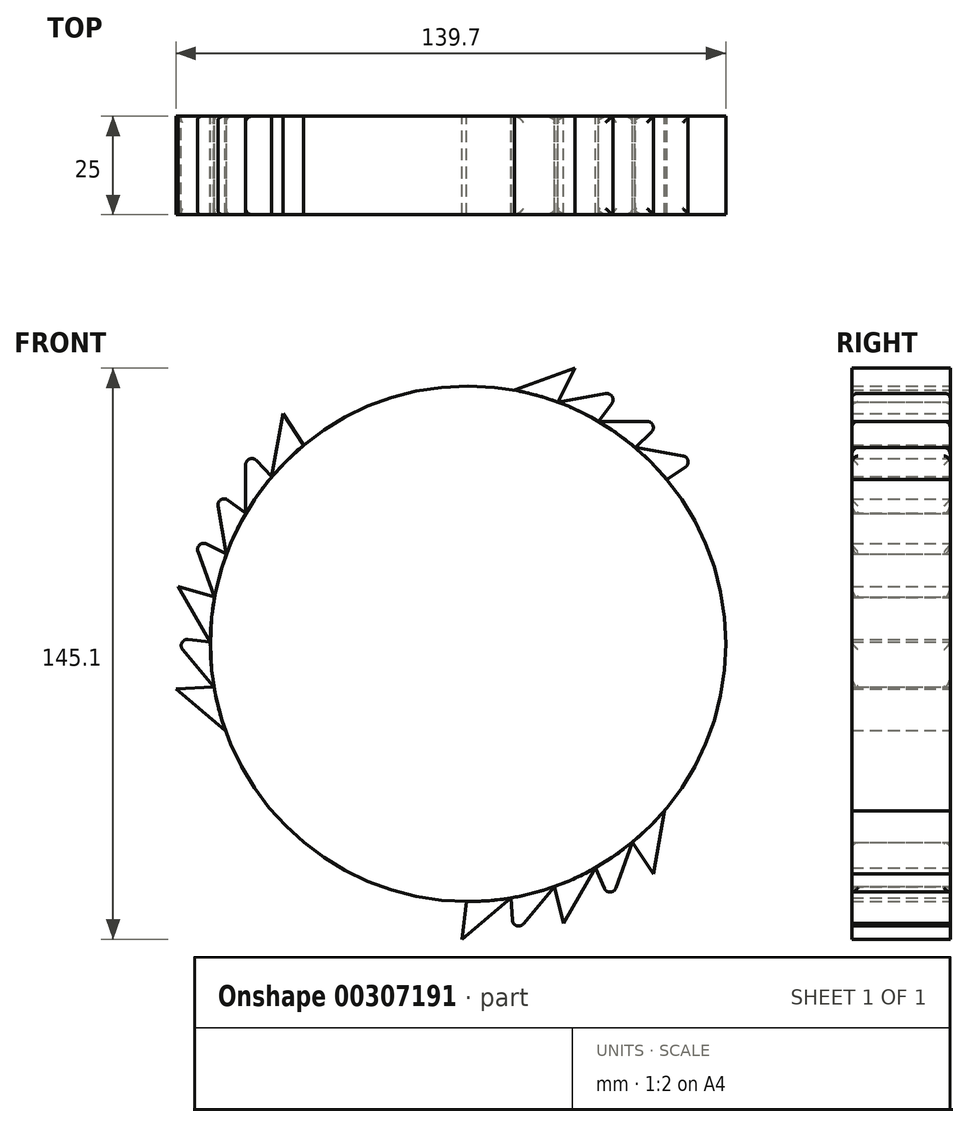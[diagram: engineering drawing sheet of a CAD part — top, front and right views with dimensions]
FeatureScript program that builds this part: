
annotation { "Feature Type Name" : "Feature", "Feature Type Description" : "" }
export const myFeature = defineFeature(function(context is Context, id is Id, definition is map)
    precondition{}
    {
        {
            var Q0;
            Q0=qCreatedBy(makeId("Front.planeOp"),FACE);
            var sketch = newSketch(context, id + "F0", { "sketchPlane" : qUnion([Q0])});
            skCircle(sketch, "E0", {"center": v(0, 0) * mm, "radius": 65.49 * mm});
            skLineSegment(sketch, "E1", {"start": v(33.09, 56.51) * mm, "end": v(49.45, 56.51) * mm});
            skLineSegment(sketch, "E2", {"start": v(49.45, 56.51) * mm, "end": v(42.44, 49.87) * mm});
            skLineSegment(sketch, "E3.1.1", {"start": v(-73.67, 14.57) * mm, "end": v(-64.4, 11.82) * mm});
            skLineSegment(sketch, "E3.1.2", {"start": v(-65.48, 0.4) * mm, "end": v(-73.67, 14.57) * mm});
            skLineSegment(sketch, "E3.2.1", {"start": v(24.21, -71.08) * mm, "end": v(21.97, -61.7) * mm});
            skLineSegment(sketch, "E3.2.2", {"start": v(32.4, -56.91) * mm, "end": v(24.21, -71.08) * mm});
            skLineSegment(sketch, "E4.1.0", {"start": v(38.89, 64.24) * mm, "end": v(33.14, 56.48) * mm});
            skLineSegment(sketch, "E4.1.1", {"start": v(22.77, 61.4) * mm, "end": v(38.89, 64.24) * mm});
            skLineSegment(sketch, "E4.1.3", {"start": v(-64.56, -10.98) * mm, "end": v(-75.08, 1.56) * mm});
            skLineSegment(sketch, "E4.1.5", {"start": v(41.79, -50.42) * mm, "end": v(36.19, -65.8) * mm});
            skLineSegment(sketch, "E4.1.6", {"start": v(-75.08, 1.56) * mm, "end": v(-65.48, 0.46) * mm});
            skLineSegment(sketch, "E4.1.7", {"start": v(36.19, -65.8) * mm, "end": v(32.34, -56.94) * mm});
            skLineSegment(sketch, "E4.2.0", {"start": v(47.07, -58.51) * mm, "end": v(41.74, -50.46) * mm});
            skLineSegment(sketch, "E4.2.1", {"start": v(49.9, -42.4) * mm, "end": v(47.07, -58.51) * mm});
            skLineSegment(sketch, "E4.2.3", {"start": v(11.77, 64.42) * mm, "end": v(27.14, 70.02) * mm});
            skLineSegment(sketch, "E4.2.5", {"start": v(-61.67, -22.02) * mm, "end": v(-74.2, -11.5) * mm});
            skLineSegment(sketch, "E4.2.6", {"start": v(27.14, 70.02) * mm, "end": v(22.83, 61.38) * mm});
            skLineSegment(sketch, "E4.2.7", {"start": v(-74.2, -11.5) * mm, "end": v(-64.57, -10.92) * mm});
            skLineSegment(sketch, "E4.anchor1", {"start": v(0, 0) * mm, "end": v(-65.48, 0.4) * mm, "construction": true});
            skLineSegment(sketch, "E4.anchor2", {"start": v(0, 0) * mm, "end": v(49.9, -42.4) * mm, "construction": true});
            skLineSegment(sketch, "E5.1.1", {"start": v(-71.08, -24.21) * mm, "end": v(-61.7, -21.97) * mm});
            skLineSegment(sketch, "E5.1.2", {"start": v(14.57, 73.67) * mm, "end": v(11.82, 64.4) * mm});
            skLineSegment(sketch, "E5.1.3", {"start": v(-56.91, -32.4) * mm, "end": v(-71.08, -24.21) * mm});
            skLineSegment(sketch, "E5.1.4", {"start": v(-50.42, -41.79) * mm, "end": v(-65.8, -36.19) * mm});
            skLineSegment(sketch, "E5.1.6", {"start": v(-65.8, -36.19) * mm, "end": v(-56.94, -32.34) * mm});
            skLineSegment(sketch, "E5.1.7", {"start": v(-10.98, 64.56) * mm, "end": v(1.56, 75.08) * mm});
            skLineSegment(sketch, "E5.1.9", {"start": v(1.56, 75.08) * mm, "end": v(0.46, 65.48) * mm});
            skLineSegment(sketch, "E5.1.10", {"start": v(0, 0) * mm, "end": v(-50.42, -41.79) * mm, "construction": true});
            skLineSegment(sketch, "E5.1.12", {"start": v(0, 0) * mm, "end": v(11.77, 64.42) * mm, "construction": true});
            skLineSegment(sketch, "E5.1.13", {"start": v(0.4, 65.48) * mm, "end": v(14.57, 73.67) * mm});
            skLineSegment(sketch, "E5.1.14", {"start": v(56.51, -33.09) * mm, "end": v(56.51, -49.45) * mm});
            skLineSegment(sketch, "E5.1.15", {"start": v(56.51, -49.45) * mm, "end": v(49.87, -42.44) * mm});
            skLineSegment(sketch, "E5.2.0", {"start": v(-50.42, -41.79) * mm, "end": v(-65.8, -36.19) * mm});
            skLineSegment(sketch, "E5.2.1", {"start": v(-11.5, 74.2) * mm, "end": v(-10.92, 64.57) * mm});
            skLineSegment(sketch, "E5.2.2", {"start": v(70.02, -27.14) * mm, "end": v(61.38, -22.83) * mm});
            skLineSegment(sketch, "E5.2.3", {"start": v(-22.02, 61.67) * mm, "end": v(-11.5, 74.2) * mm});
            skLineSegment(sketch, "E5.2.4", {"start": v(-32.4, 56.91) * mm, "end": v(-24.21, 71.08) * mm});
            skLineSegment(sketch, "E5.2.5", {"start": v(64.24, -38.89) * mm, "end": v(56.48, -33.14) * mm});
            skLineSegment(sketch, "E5.2.6", {"start": v(-24.21, 71.08) * mm, "end": v(-21.97, 61.7) * mm});
            skLineSegment(sketch, "E5.2.7", {"start": v(65.48, -0.4) * mm, "end": v(73.67, -14.57) * mm});
            skLineSegment(sketch, "E5.2.9", {"start": v(73.67, -14.57) * mm, "end": v(64.4, -11.82) * mm});
            skLineSegment(sketch, "E5.2.10", {"start": v(0, 0) * mm, "end": v(-32.4, 56.91) * mm, "construction": true});
            skLineSegment(sketch, "E5.2.12", {"start": v(0, 0) * mm, "end": v(61.4, -22.77) * mm, "construction": true});
            skLineSegment(sketch, "E5.2.13", {"start": v(64.42, -11.77) * mm, "end": v(70.02, -27.14) * mm});
            skLineSegment(sketch, "E5.2.14", {"start": v(-42.4, -49.9) * mm, "end": v(-58.51, -47.07) * mm});
            skLineSegment(sketch, "E5.2.15", {"start": v(-58.51, -47.07) * mm, "end": v(-50.46, -41.74) * mm});
            skLineSegment(sketch, "E5.2.16", {"start": v(-10.98, 64.56) * mm, "end": v(1.56, 75.08) * mm});
            skLineSegment(sketch, "E5.2.17", {"start": v(1.56, 75.08) * mm, "end": v(0.46, 65.48) * mm});
            skLineSegment(sketch, "E5.2.18", {"start": v(-65.8, -36.19) * mm, "end": v(-56.94, -32.34) * mm});
            skLineSegment(sketch, "E5.2.19", {"start": v(61.4, -22.77) * mm, "end": v(64.24, -38.89) * mm});
            skLineSegment(sketch, "E5.anchor1", {"start": v(0, 0) * mm, "end": v(-74.2, -11.5) * mm, "construction": true});
            skLineSegment(sketch, "E5.anchor2", {"start": v(0, 0) * mm, "end": v(73.67, -14.57) * mm, "construction": true});
            skLineSegment(sketch, "E6.1.0", {"start": v(0, 0) * mm, "end": v(-14.57, -73.67) * mm, "construction": true});
            skLineSegment(sketch, "E6.1.1", {"start": v(-38.89, -64.24) * mm, "end": v(-33.14, -56.48) * mm});
            skLineSegment(sketch, "E6.1.2", {"start": v(-11.77, -64.42) * mm, "end": v(-27.14, -70.02) * mm});
            skLineSegment(sketch, "E6.1.3", {"start": v(56.91, 32.4) * mm, "end": v(71.08, 24.21) * mm});
            skLineSegment(sketch, "E6.1.4", {"start": v(0, 0) * mm, "end": v(-42.4, -49.9) * mm, "construction": true});
            skLineSegment(sketch, "E6.1.5", {"start": v(-49.45, -56.51) * mm, "end": v(-42.44, -49.87) * mm});
            skLineSegment(sketch, "E6.1.6", {"start": v(0, 0) * mm, "end": v(0.4, 65.48) * mm, "construction": true});
            skLineSegment(sketch, "E6.1.10", {"start": v(0, 0) * mm, "end": v(56.91, 32.4) * mm, "construction": true});
            skLineSegment(sketch, "E6.1.12", {"start": v(-36.19, 65.8) * mm, "end": v(-32.34, 56.94) * mm});
            skLineSegment(sketch, "E6.1.13", {"start": v(74.2, 11.5) * mm, "end": v(64.57, 10.92) * mm});
            skLineSegment(sketch, "E6.1.15", {"start": v(-41.79, 50.42) * mm, "end": v(-36.19, 65.8) * mm});
            skLineSegment(sketch, "E6.1.16", {"start": v(-14.57, -73.67) * mm, "end": v(-11.82, -64.4) * mm});
            skLineSegment(sketch, "E6.1.17", {"start": v(75.08, -1.56) * mm, "end": v(65.48, -0.46) * mm});
            skLineSegment(sketch, "E6.1.20", {"start": v(64.56, 10.98) * mm, "end": v(75.08, -1.56) * mm});
            skLineSegment(sketch, "E6.1.21", {"start": v(0, 0) * mm, "end": v(-41.79, 50.42) * mm, "construction": true});
            skLineSegment(sketch, "E6.1.36", {"start": v(-47.07, 58.51) * mm, "end": v(-41.74, 50.46) * mm});
            skLineSegment(sketch, "E6.1.37", {"start": v(-0.4, -65.48) * mm, "end": v(-14.57, -73.67) * mm});
            skLineSegment(sketch, "E6.1.40", {"start": v(-49.9, 42.4) * mm, "end": v(-47.07, 58.51) * mm});
            skLineSegment(sketch, "E6.1.41", {"start": v(71.08, 24.21) * mm, "end": v(61.7, 21.97) * mm});
            skLineSegment(sketch, "E6.1.43", {"start": v(-27.14, -70.02) * mm, "end": v(-22.83, -61.38) * mm});
            skLineSegment(sketch, "E6.1.44", {"start": v(-33.09, -56.51) * mm, "end": v(-49.45, -56.51) * mm});
            skLineSegment(sketch, "E6.1.45", {"start": v(-22.77, -61.4) * mm, "end": v(-38.89, -64.24) * mm});
            skLineSegment(sketch, "E6.1.46", {"start": v(0, 0) * mm, "end": v(-11.5, 74.2) * mm, "construction": true});
            skLineSegment(sketch, "E6.1.47", {"start": v(0, 0) * mm, "end": v(-22.77, -61.4) * mm, "construction": true});
            skLineSegment(sketch, "E6.1.48", {"start": v(61.67, 22.02) * mm, "end": v(74.2, 11.5) * mm});
            skLineSegment(sketch, "E6.1.53", {"start": v(-41.79, 50.42) * mm, "end": v(-36.19, 65.8) * mm});
            skLineSegment(sketch, "E6.1.55", {"start": v(75.08, -1.56) * mm, "end": v(65.48, -0.46) * mm});
            skLineSegment(sketch, "E6.1.58", {"start": v(64.56, 10.98) * mm, "end": v(75.08, -1.56) * mm});
            skLineSegment(sketch, "E6.1.60", {"start": v(-36.19, 65.8) * mm, "end": v(-32.34, 56.94) * mm});
            skLineSegment(sketch, "E6.1.97", {"start": v(0, 0) * mm, "end": v(64.42, -11.77) * mm, "construction": true});
            skLineSegment(sketch, "E6.2.0", {"start": v(0, 0) * mm, "end": v(-73.67, 14.57) * mm, "construction": true});
            skLineSegment(sketch, "E6.2.1", {"start": v(-64.24, 38.89) * mm, "end": v(-56.48, 33.14) * mm});
            skLineSegment(sketch, "E6.2.2", {"start": v(-64.42, 11.77) * mm, "end": v(-70.02, 27.14) * mm});
            skLineSegment(sketch, "E6.2.4", {"start": v(0, 0) * mm, "end": v(-49.9, 42.4) * mm, "construction": true});
            skLineSegment(sketch, "E6.2.5", {"start": v(-56.51, 49.45) * mm, "end": v(-49.87, 42.44) * mm});
            skLineSegment(sketch, "E6.2.6", {"start": v(0, 0) * mm, "end": v(65.48, -0.4) * mm, "construction": true});
            skLineSegment(sketch, "E6.2.8", {"start": v(-27.14, -70.02) * mm, "end": v(-22.83, -61.38) * mm});
            skLineSegment(sketch, "E6.2.10", {"start": v(0, 0) * mm, "end": v(32.4, -56.91) * mm, "construction": true});
            skLineSegment(sketch, "E6.2.11", {"start": v(-47.07, 58.51) * mm, "end": v(-41.74, 50.46) * mm});
            skLineSegment(sketch, "E6.2.12", {"start": v(65.8, 36.19) * mm, "end": v(56.94, 32.34) * mm});
            skLineSegment(sketch, "E6.2.13", {"start": v(11.5, -74.2) * mm, "end": v(10.92, -64.57) * mm});
            skLineSegment(sketch, "E6.2.14", {"start": v(-0.4, -65.48) * mm, "end": v(-14.57, -73.67) * mm});
            skLineSegment(sketch, "E6.2.15", {"start": v(50.42, 41.79) * mm, "end": v(65.8, 36.19) * mm});
            skLineSegment(sketch, "E6.2.17", {"start": v(-1.56, -75.08) * mm, "end": v(-0.46, -65.48) * mm});
            skLineSegment(sketch, "E6.2.18", {"start": v(74.2, 11.5) * mm, "end": v(64.57, 10.92) * mm});
            skLineSegment(sketch, "E6.2.19", {"start": v(56.91, 32.4) * mm, "end": v(71.08, 24.21) * mm});
            skLineSegment(sketch, "E6.2.20", {"start": v(10.98, -64.56) * mm, "end": v(-1.56, -75.08) * mm});
            skLineSegment(sketch, "E6.2.21", {"start": v(0, 0) * mm, "end": v(50.42, 41.79) * mm, "construction": true});
            skLineSegment(sketch, "E6.2.22", {"start": v(64.56, 10.98) * mm, "end": v(75.08, -1.56) * mm});
            skLineSegment(sketch, "E6.2.23", {"start": v(-22.77, -61.4) * mm, "end": v(-38.89, -64.24) * mm});
            skLineSegment(sketch, "E6.2.24", {"start": v(-38.89, -64.24) * mm, "end": v(-33.14, -56.48) * mm});
            skLineSegment(sketch, "E6.2.29", {"start": v(-49.45, -56.51) * mm, "end": v(-42.44, -49.87) * mm});
            skLineSegment(sketch, "E6.2.30", {"start": v(-33.09, -56.51) * mm, "end": v(-49.45, -56.51) * mm});
            skLineSegment(sketch, "E6.2.31", {"start": v(-36.19, 65.8) * mm, "end": v(-32.34, 56.94) * mm});
            skLineSegment(sketch, "E6.2.32", {"start": v(75.08, -1.56) * mm, "end": v(65.48, -0.46) * mm});
            skLineSegment(sketch, "E6.2.33", {"start": v(-41.79, 50.42) * mm, "end": v(-36.19, 65.8) * mm});
            skLineSegment(sketch, "E6.2.34", {"start": v(-14.57, -73.67) * mm, "end": v(-11.82, -64.4) * mm});
            skLineSegment(sketch, "E6.2.35", {"start": v(-11.77, -64.42) * mm, "end": v(-27.14, -70.02) * mm});
            skLineSegment(sketch, "E6.2.36", {"start": v(58.51, 47.07) * mm, "end": v(50.46, 41.74) * mm});
            skLineSegment(sketch, "E6.2.38", {"start": v(61.67, 22.02) * mm, "end": v(74.2, 11.5) * mm});
            skLineSegment(sketch, "E6.2.39", {"start": v(71.08, 24.21) * mm, "end": v(61.7, 21.97) * mm});
            skLineSegment(sketch, "E6.2.40", {"start": v(42.4, 49.9) * mm, "end": v(58.51, 47.07) * mm});
            skLineSegment(sketch, "E6.2.42", {"start": v(-49.9, 42.4) * mm, "end": v(-47.07, 58.51) * mm});
            skLineSegment(sketch, "E6.2.43", {"start": v(-70.02, 27.14) * mm, "end": v(-61.38, 22.83) * mm});
            skLineSegment(sketch, "E6.2.44", {"start": v(-56.51, 33.09) * mm, "end": v(-56.51, 49.45) * mm});
            skLineSegment(sketch, "E6.2.45", {"start": v(-61.4, 22.77) * mm, "end": v(-64.24, 38.89) * mm});
            skLineSegment(sketch, "E6.2.46", {"start": v(0, 0) * mm, "end": v(74.2, 11.5) * mm, "construction": true});
            skLineSegment(sketch, "E6.2.47", {"start": v(0, 0) * mm, "end": v(-61.4, 22.77) * mm, "construction": true});
            skLineSegment(sketch, "E6.2.48", {"start": v(22.02, -61.67) * mm, "end": v(11.5, -74.2) * mm});
            skLineSegment(sketch, "E6.2.49", {"start": v(74.2, 11.5) * mm, "end": v(64.57, 10.92) * mm});
            skLineSegment(sketch, "E6.2.50", {"start": v(61.67, 22.02) * mm, "end": v(74.2, 11.5) * mm});
            skLineSegment(sketch, "E6.2.53", {"start": v(50.42, 41.79) * mm, "end": v(65.8, 36.19) * mm});
            skLineSegment(sketch, "E6.2.54", {"start": v(-27.14, -70.02) * mm, "end": v(-22.83, -61.38) * mm});
            skLineSegment(sketch, "E6.2.55", {"start": v(-1.56, -75.08) * mm, "end": v(-0.46, -65.48) * mm});
            skLineSegment(sketch, "E6.2.56", {"start": v(-47.07, 58.51) * mm, "end": v(-41.74, 50.46) * mm});
            skLineSegment(sketch, "E6.2.57", {"start": v(-11.77, -64.42) * mm, "end": v(-27.14, -70.02) * mm});
            skLineSegment(sketch, "E6.2.58", {"start": v(10.98, -64.56) * mm, "end": v(-1.56, -75.08) * mm});
            skLineSegment(sketch, "E6.2.59", {"start": v(-49.9, 42.4) * mm, "end": v(-47.07, 58.51) * mm});
            skLineSegment(sketch, "E6.2.60", {"start": v(65.8, 36.19) * mm, "end": v(56.94, 32.34) * mm});
            skLineSegment(sketch, "E6.2.97", {"start": v(0, 0) * mm, "end": v(-11.77, -64.42) * mm, "construction": true});
            skLineSegment(sketch, "E6.anchor1", {"start": v(0, 0) * mm, "end": v(-58.51, -47.07) * mm, "construction": true});
            skLineSegment(sketch, "E6.anchor2", {"start": v(0, 0) * mm, "end": v(58.51, 47.07) * mm, "construction": true});
            skSolve(sketch);
        }
        {
            var Q0;
            {var subQ0=sQuery(id+"F0.wireOp",EDGE,"E0");var subQ33=makeQuery(id+"F0.imprint","INTERSECT",VERTEX,{"derivedFrom":[sQuery(id+"F0.wireOp",EDGE,"E5.2.5"),subQ0]});Q0=makeQuery(id+"F0.imprint","IMPRINT",FACE,{"disambiguationData":[TD([[makeQuery(id+"F0.imprint","IMPRINT",EDGE,{"disambiguationData":[TD([[subQ33,-1.0]])],"derivedFrom":subQ0}),1.0]])]});}
            extrude(context, id + "F1", {"entities" : qUnion([Q0]), "depth" : 25 * mm});
        }
        {
            var Q0;
            {var subQ3=sQuery(id+"F0.wireOp",EDGE,"E5.2.3");var subQ5=sQuery(id+"F0.wireOp",EDGE,"E0");var subQ9=makeQuery(id+"F0.imprint","INTERSECT",VERTEX,{"derivedFrom":[subQ3,subQ5]});Q0=makeQuery(id+"F0.imprint","IMPRINT",FACE,{"disambiguationData":[TD([[makeQuery(id+"F0.imprint","IMPRINT",EDGE,{"disambiguationData":[TD([[subQ9,-1.0]])],"derivedFrom":subQ3}),1.0]])]});}
            var Q1;
            {var subQ0=sQuery(id+"F0.wireOp",EDGE,"E0");var subQ7=sQuery(id+"F0.wireOp",EDGE,"E5.2.4");var subQ9=makeQuery(id+"F0.imprint","INTERSECT",VERTEX,{"derivedFrom":[subQ7,subQ0]});Q1=makeQuery(id+"F0.imprint","IMPRINT",FACE,{"disambiguationData":[TD([[makeQuery(id+"F0.imprint","IMPRINT",EDGE,{"disambiguationData":[TD([[subQ9,-1.0]])],"derivedFrom":subQ7}),1.0]])]});}
            var Q2;
            {var subQ5=sQuery(id+"F0.wireOp",EDGE,"E0");var subQ7=sQuery(id+"F0.wireOp",EDGE,"E6.2.5");var subQ9=makeQuery(id+"F0.imprint","INTERSECT",VERTEX,{"derivedFrom":[subQ7,subQ5]});Q2=makeQuery(id+"F0.imprint","IMPRINT",FACE,{"disambiguationData":[TD([[makeQuery(id+"F0.imprint","IMPRINT",EDGE,{"disambiguationData":[TD([[subQ9,1.0]])],"derivedFrom":subQ7}),1.0]])]});}
            var Q3;
            {var subQ0=sQuery(id+"F0.wireOp",EDGE,"E0");var subQ7=sQuery(id+"F0.wireOp",EDGE,"E5.1.7");var subQ9=makeQuery(id+"F0.imprint","INTERSECT",VERTEX,{"derivedFrom":[subQ7,subQ0]});Q3=makeQuery(id+"F0.imprint","IMPRINT",FACE,{"disambiguationData":[TD([[makeQuery(id+"F0.imprint","IMPRINT",EDGE,{"disambiguationData":[TD([[subQ9,-1.0]])],"derivedFrom":subQ7}),1.0]])]});}
            var Q4;
            {var subQ3=sQuery(id+"F0.wireOp",EDGE,"E5.1.7");var subQ5=sQuery(id+"F0.wireOp",EDGE,"E5.1.9");var subQ6=makeQuery(id+"F0.imprint","INTERSECT",VERTEX,{"derivedFrom":[subQ3,subQ5]});Q4=makeQuery(id+"F0.imprint","IMPRINT",FACE,{"disambiguationData":[TD([[makeQuery(id+"F0.imprint","IMPRINT",EDGE,{"disambiguationData":[TD([[subQ6,1.0]])],"derivedFrom":subQ3}),-1.0]])]});}
            var Q5;
            {var subQ3=sQuery(id+"F0.wireOp",EDGE,"E4.2.3");var subQ5=sQuery(id+"F0.wireOp",EDGE,"E0");var subQ9=makeQuery(id+"F0.imprint","INTERSECT",VERTEX,{"derivedFrom":[subQ3,subQ5]});Q5=makeQuery(id+"F0.imprint","IMPRINT",FACE,{"disambiguationData":[TD([[makeQuery(id+"F0.imprint","IMPRINT",EDGE,{"disambiguationData":[TD([[subQ9,-1.0]])],"derivedFrom":subQ3}),1.0]])]});}
            var Q6;
            {var subQ5=sQuery(id+"F0.wireOp",EDGE,"E4.1.1");var subQ7=sQuery(id+"F0.wireOp",EDGE,"E0");var subQ9=makeQuery(id+"F0.imprint","INTERSECT",VERTEX,{"derivedFrom":[subQ5,subQ7]});Q6=makeQuery(id+"F0.imprint","IMPRINT",FACE,{"disambiguationData":[TD([[makeQuery(id+"F0.imprint","IMPRINT",EDGE,{"disambiguationData":[TD([[subQ9,-1.0]])],"derivedFrom":subQ5}),1.0]])]});}
            var Q7;
            {var subQ5=sQuery(id+"F0.wireOp",EDGE,"E0");var subQ7=sQuery(id+"F0.wireOp",EDGE,"E1");var subQ9=makeQuery(id+"F0.imprint","INTERSECT",VERTEX,{"derivedFrom":[subQ7,subQ5]});Q7=makeQuery(id+"F0.imprint","IMPRINT",FACE,{"disambiguationData":[TD([[makeQuery(id+"F0.imprint","IMPRINT",EDGE,{"disambiguationData":[TD([[subQ9,-1.0]])],"derivedFrom":subQ7}),1.0]])]});}
            var Q8;
            {var subQ3=sQuery(id+"F0.wireOp",EDGE,"E1");var subQ7=sQuery(id+"F0.wireOp",EDGE,"E2");var subQ9=makeQuery(id+"F0.imprint","INTERSECT",VERTEX,{"derivedFrom":[subQ3,subQ7]});Q8=makeQuery(id+"F0.imprint","IMPRINT",FACE,{"disambiguationData":[TD([[makeQuery(id+"F0.imprint","IMPRINT",EDGE,{"disambiguationData":[TD([[subQ9,1.0]])],"derivedFrom":subQ3}),-1.0]])]});}
            var Q9;
            {var subQ5=sQuery(id+"F0.wireOp",EDGE,"E0");var subQ7=sQuery(id+"F0.wireOp",EDGE,"E2");var subQ9=makeQuery(id+"F0.imprint","INTERSECT",VERTEX,{"derivedFrom":[subQ7,subQ5]});Q9=makeQuery(id+"F0.imprint","IMPRINT",FACE,{"disambiguationData":[TD([[makeQuery(id+"F0.imprint","IMPRINT",EDGE,{"disambiguationData":[TD([[subQ9,1.0]])],"derivedFrom":subQ7}),1.0]])]});}
            var Q10;
            {var subQ5=sQuery(id+"F0.wireOp",EDGE,"E0");var subQ7=sQuery(id+"F0.wireOp",EDGE,"E6.2.19");var subQ9=makeQuery(id+"F0.imprint","INTERSECT",VERTEX,{"derivedFrom":[subQ7,subQ5]});Q10=makeQuery(id+"F0.imprint","IMPRINT",FACE,{"disambiguationData":[TD([[makeQuery(id+"F0.imprint","IMPRINT",EDGE,{"disambiguationData":[TD([[subQ9,-1.0]])],"derivedFrom":subQ7}),1.0]])]});}
            var Q11;
            {var subQ3=sQuery(id+"F0.wireOp",EDGE,"E6.2.19");var subQ5=sQuery(id+"F0.wireOp",EDGE,"E6.2.39");var subQ6=makeQuery(id+"F0.imprint","INTERSECT",VERTEX,{"derivedFrom":[subQ3,subQ5]});Q11=makeQuery(id+"F0.imprint","IMPRINT",FACE,{"disambiguationData":[TD([[makeQuery(id+"F0.imprint","IMPRINT",EDGE,{"disambiguationData":[TD([[subQ6,1.0]])],"derivedFrom":subQ3}),-1.0]])]});}
            var Q12;
            {var subQ5=sQuery(id+"F0.wireOp",EDGE,"E6.2.22");var subQ7=sQuery(id+"F0.wireOp",EDGE,"E0");var subQ8=makeQuery(id+"F0.imprint","INTERSECT",VERTEX,{"derivedFrom":[subQ5,subQ7]});Q12=makeQuery(id+"F0.imprint","IMPRINT",FACE,{"disambiguationData":[TD([[makeQuery(id+"F0.imprint","IMPRINT",EDGE,{"disambiguationData":[TD([[subQ8,-1.0]])],"derivedFrom":subQ5}),1.0]])]});}
            var Q13;
            {var subQ3=sQuery(id+"F0.wireOp",EDGE,"E6.2.22");var subQ5=sQuery(id+"F0.wireOp",EDGE,"E6.2.32");var subQ6=makeQuery(id+"F0.imprint","INTERSECT",VERTEX,{"derivedFrom":[subQ3,subQ5]});Q13=makeQuery(id+"F0.imprint","IMPRINT",FACE,{"disambiguationData":[TD([[makeQuery(id+"F0.imprint","IMPRINT",EDGE,{"disambiguationData":[TD([[subQ6,1.0]])],"derivedFrom":subQ3}),-1.0]])]});}
            var Q14;
            {var subQ3=sQuery(id+"F0.wireOp",EDGE,"E5.2.13");var subQ5=sQuery(id+"F0.wireOp",EDGE,"E0");var subQ9=makeQuery(id+"F0.imprint","INTERSECT",VERTEX,{"derivedFrom":[subQ3,subQ5]});Q14=makeQuery(id+"F0.imprint","IMPRINT",FACE,{"disambiguationData":[TD([[makeQuery(id+"F0.imprint","IMPRINT",EDGE,{"disambiguationData":[TD([[subQ9,-1.0]])],"derivedFrom":subQ3}),1.0]])]});}
            var Q15;
            {var subQ0=sQuery(id+"F0.wireOp",EDGE,"E0");var subQ7=sQuery(id+"F0.wireOp",EDGE,"E5.2.19");var subQ9=makeQuery(id+"F0.imprint","INTERSECT",VERTEX,{"derivedFrom":[subQ7,subQ0]});Q15=makeQuery(id+"F0.imprint","IMPRINT",FACE,{"disambiguationData":[TD([[makeQuery(id+"F0.imprint","IMPRINT",EDGE,{"disambiguationData":[TD([[subQ9,-1.0]])],"derivedFrom":subQ7}),1.0]])]});}
            var Q16;
            {var subQ3=sQuery(id+"F0.wireOp",EDGE,"E5.2.5");var subQ7=sQuery(id+"F0.wireOp",EDGE,"E5.2.19");var subQ9=makeQuery(id+"F0.imprint","INTERSECT",VERTEX,{"derivedFrom":[subQ7,subQ3]});Q16=makeQuery(id+"F0.imprint","IMPRINT",FACE,{"disambiguationData":[TD([[makeQuery(id+"F0.imprint","IMPRINT",EDGE,{"disambiguationData":[TD([[subQ9,1.0]])],"derivedFrom":subQ7}),-1.0]])]});}
            var Q17;
            {var subQ5=sQuery(id+"F0.wireOp",EDGE,"E4.2.1");var subQ7=sQuery(id+"F0.wireOp",EDGE,"E0");var subQ9=makeQuery(id+"F0.imprint","INTERSECT",VERTEX,{"derivedFrom":[subQ5,subQ7]});Q17=makeQuery(id+"F0.imprint","IMPRINT",FACE,{"disambiguationData":[TD([[makeQuery(id+"F0.imprint","IMPRINT",EDGE,{"disambiguationData":[TD([[subQ9,-1.0]])],"derivedFrom":subQ5}),1.0]])]});}
            var Q18;
            {var subQ0=sQuery(id+"F0.wireOp",EDGE,"E0");var subQ5=sQuery(id+"F0.wireOp",EDGE,"E4.1.5");var subQ6=makeQuery(id+"F0.imprint","INTERSECT",VERTEX,{"derivedFrom":[subQ5,subQ0]});Q18=makeQuery(id+"F0.imprint","IMPRINT",FACE,{"disambiguationData":[TD([[makeQuery(id+"F0.imprint","IMPRINT",EDGE,{"disambiguationData":[TD([[subQ6,-1.0]])],"derivedFrom":subQ5}),1.0]])]});}
            var Q19;
            {var subQ3=sQuery(id+"F0.wireOp",EDGE,"E4.1.7");var subQ7=sQuery(id+"F0.wireOp",EDGE,"E4.1.5");var subQ9=makeQuery(id+"F0.imprint","INTERSECT",VERTEX,{"derivedFrom":[subQ7,subQ3]});Q19=makeQuery(id+"F0.imprint","IMPRINT",FACE,{"disambiguationData":[TD([[makeQuery(id+"F0.imprint","IMPRINT",EDGE,{"disambiguationData":[TD([[subQ9,1.0]])],"derivedFrom":subQ7}),-1.0]])]});}
            var Q20;
            {var subQ0=sQuery(id+"F0.wireOp",EDGE,"E0");var subQ7=sQuery(id+"F0.wireOp",EDGE,"E4.1.7");var subQ8=makeQuery(id+"F0.imprint","INTERSECT",VERTEX,{"derivedFrom":[subQ7,subQ0]});Q20=makeQuery(id+"F0.imprint","IMPRINT",FACE,{"disambiguationData":[TD([[makeQuery(id+"F0.imprint","IMPRINT",EDGE,{"disambiguationData":[TD([[subQ8,1.0]])],"derivedFrom":subQ7}),1.0]])]});}
            var Q21;
            {var subQ3=sQuery(id+"F0.wireOp",EDGE,"E6.2.13");var subQ5=sQuery(id+"F0.wireOp",EDGE,"E6.2.48");var subQ6=makeQuery(id+"F0.imprint","INTERSECT",VERTEX,{"derivedFrom":[subQ3,subQ5]});Q21=makeQuery(id+"F0.imprint","IMPRINT",FACE,{"disambiguationData":[TD([[makeQuery(id+"F0.imprint","IMPRINT",EDGE,{"disambiguationData":[TD([[subQ6,-1.0]])],"derivedFrom":subQ3}),-1.0]])]});}
            var Q22;
            {var subQ5=sQuery(id+"F0.wireOp",EDGE,"E6.2.13");var subQ7=sQuery(id+"F0.wireOp",EDGE,"E0");var subQ8=makeQuery(id+"F0.imprint","INTERSECT",VERTEX,{"derivedFrom":[subQ5,subQ7]});Q22=makeQuery(id+"F0.imprint","IMPRINT",FACE,{"disambiguationData":[TD([[makeQuery(id+"F0.imprint","IMPRINT",EDGE,{"disambiguationData":[TD([[subQ8,1.0]])],"derivedFrom":subQ5}),1.0]])]});}
            var Q23;
            {var subQ3=sQuery(id+"F0.wireOp",EDGE,"E6.2.34");var subQ7=sQuery(id+"F0.wireOp",EDGE,"E6.2.14");var subQ9=makeQuery(id+"F0.imprint","INTERSECT",VERTEX,{"derivedFrom":[subQ7,subQ3]});Q23=makeQuery(id+"F0.imprint","IMPRINT",FACE,{"disambiguationData":[TD([[makeQuery(id+"F0.imprint","IMPRINT",EDGE,{"disambiguationData":[TD([[subQ9,1.0]])],"derivedFrom":subQ7}),-1.0]])]});}
            var Q24;
            {var subQ3=sQuery(id+"F0.wireOp",EDGE,"E6.2.23");var subQ5=sQuery(id+"F0.wireOp",EDGE,"E0");var subQ9=makeQuery(id+"F0.imprint","INTERSECT",VERTEX,{"derivedFrom":[subQ3,subQ5]});Q24=makeQuery(id+"F0.imprint","IMPRINT",FACE,{"disambiguationData":[TD([[makeQuery(id+"F0.imprint","IMPRINT",EDGE,{"disambiguationData":[TD([[subQ9,-1.0]])],"derivedFrom":subQ3}),1.0]])]});}
            var Q25;
            {var subQ3=sQuery(id+"F0.wireOp",EDGE,"E6.2.23");var subQ7=sQuery(id+"F0.wireOp",EDGE,"E6.2.24");var subQ9=makeQuery(id+"F0.imprint","INTERSECT",VERTEX,{"derivedFrom":[subQ3,subQ7]});Q25=makeQuery(id+"F0.imprint","IMPRINT",FACE,{"disambiguationData":[TD([[makeQuery(id+"F0.imprint","IMPRINT",EDGE,{"disambiguationData":[TD([[subQ9,1.0]])],"derivedFrom":subQ3}),-1.0]])]});}
            var Q26;
            {var subQ3=sQuery(id+"F0.wireOp",EDGE,"E5.2.14");var subQ5=sQuery(id+"F0.wireOp",EDGE,"E0");var subQ9=makeQuery(id+"F0.imprint","INTERSECT",VERTEX,{"derivedFrom":[subQ3,subQ5]});Q26=makeQuery(id+"F0.imprint","IMPRINT",FACE,{"disambiguationData":[TD([[makeQuery(id+"F0.imprint","IMPRINT",EDGE,{"disambiguationData":[TD([[subQ9,-1.0]])],"derivedFrom":subQ3}),1.0]])]});}
            var Q27;
            {var subQ5=sQuery(id+"F0.wireOp",EDGE,"E5.1.3");var subQ7=sQuery(id+"F0.wireOp",EDGE,"E0");var subQ9=makeQuery(id+"F0.imprint","INTERSECT",VERTEX,{"derivedFrom":[subQ5,subQ7]});Q27=makeQuery(id+"F0.imprint","IMPRINT",FACE,{"disambiguationData":[TD([[makeQuery(id+"F0.imprint","IMPRINT",EDGE,{"disambiguationData":[TD([[subQ9,-1.0]])],"derivedFrom":subQ5}),1.0]])]});}
            var Q28;
            {var subQ0=sQuery(id+"F0.wireOp",EDGE,"E0");var subQ7=sQuery(id+"F0.wireOp",EDGE,"E4.2.5");var subQ9=makeQuery(id+"F0.imprint","INTERSECT",VERTEX,{"derivedFrom":[subQ7,subQ0]});Q28=makeQuery(id+"F0.imprint","IMPRINT",FACE,{"disambiguationData":[TD([[makeQuery(id+"F0.imprint","IMPRINT",EDGE,{"disambiguationData":[TD([[subQ9,-1.0]])],"derivedFrom":subQ7}),1.0]])]});}
            var Q29;
            {var subQ5=sQuery(id+"F0.wireOp",EDGE,"E0");var subQ6=sQuery(id+"F0.wireOp",EDGE,"E5.1.4");var subQ7=makeQuery(id+"F0.imprint","INTERSECT",VERTEX,{"derivedFrom":[subQ6,subQ5]});Q29=makeQuery(id+"F0.imprint","IMPRINT",FACE,{"disambiguationData":[TD([[makeQuery(id+"F0.imprint","IMPRINT",EDGE,{"disambiguationData":[TD([[subQ7,-1.0]])],"derivedFrom":subQ6}),1.0]])]});}
            var Q30;
            {var subQ0=sQuery(id+"F0.wireOp",EDGE,"E0");var subQ7=sQuery(id+"F0.wireOp",EDGE,"E4.1.3");var subQ9=makeQuery(id+"F0.imprint","INTERSECT",VERTEX,{"derivedFrom":[subQ7,subQ0]});Q30=makeQuery(id+"F0.imprint","IMPRINT",FACE,{"disambiguationData":[TD([[makeQuery(id+"F0.imprint","IMPRINT",EDGE,{"disambiguationData":[TD([[subQ9,-1.0]])],"derivedFrom":subQ7}),1.0]])]});}
            var Q31;
            {var subQ3=sQuery(id+"F0.wireOp",EDGE,"E4.1.6");var subQ5=sQuery(id+"F0.wireOp",EDGE,"E4.1.3");var subQ6=makeQuery(id+"F0.imprint","INTERSECT",VERTEX,{"derivedFrom":[subQ5,subQ3]});Q31=makeQuery(id+"F0.imprint","IMPRINT",FACE,{"disambiguationData":[TD([[makeQuery(id+"F0.imprint","IMPRINT",EDGE,{"disambiguationData":[TD([[subQ6,1.0]])],"derivedFrom":subQ5}),-1.0]])]});}
            var Q32;
            {var subQ3=sQuery(id+"F0.wireOp",EDGE,"E4.1.6");var subQ7=sQuery(id+"F0.wireOp",EDGE,"E0");var subQ9=makeQuery(id+"F0.imprint","INTERSECT",VERTEX,{"derivedFrom":[subQ3,subQ7]});Q32=makeQuery(id+"F0.imprint","IMPRINT",FACE,{"disambiguationData":[TD([[makeQuery(id+"F0.imprint","IMPRINT",EDGE,{"disambiguationData":[TD([[subQ9,1.0]])],"derivedFrom":subQ3}),1.0]])]});}
            var Q33;
            {var subQ3=sQuery(id+"F0.wireOp",EDGE,"E6.2.43");var subQ5=sQuery(id+"F0.wireOp",EDGE,"E6.2.2");var subQ6=makeQuery(id+"F0.imprint","INTERSECT",VERTEX,{"derivedFrom":[subQ5,subQ3]});Q33=makeQuery(id+"F0.imprint","IMPRINT",FACE,{"disambiguationData":[TD([[makeQuery(id+"F0.imprint","IMPRINT",EDGE,{"disambiguationData":[TD([[subQ6,1.0]])],"derivedFrom":subQ5}),-1.0]])]});}
            var Q34;
            {var subQ0=sQuery(id+"F0.wireOp",EDGE,"E6.2.45");var subQ1=sQuery(id+"F0.wireOp",EDGE,"E6.2.1");var subQ2=makeQuery(id+"F0.imprint","INTERSECT",VERTEX,{"derivedFrom":[subQ1,subQ0]});Q34=makeQuery(id+"F0.imprint","IMPRINT",FACE,{"disambiguationData":[TD([[makeQuery(id+"F0.imprint","IMPRINT",EDGE,{"disambiguationData":[TD([[subQ2,-1.0]])],"derivedFrom":subQ1}),-1.0]])]});}
            var Q35;
            {var subQ3=sQuery(id+"F0.wireOp",EDGE,"E6.2.1");var subQ5=sQuery(id+"F0.wireOp",EDGE,"E0");var subQ9=makeQuery(id+"F0.imprint","INTERSECT",VERTEX,{"derivedFrom":[subQ3,subQ5]});Q35=makeQuery(id+"F0.imprint","IMPRINT",FACE,{"disambiguationData":[TD([[makeQuery(id+"F0.imprint","IMPRINT",EDGE,{"disambiguationData":[TD([[subQ9,1.0]])],"derivedFrom":subQ3}),1.0]])]});}
            extrude(context, id + "F2", {"entities" : qUnion([Q0, Q1, Q2, Q3, Q4, Q5, Q6, Q7, Q8, Q9, Q10, Q11, Q12, Q13, Q14, Q15, Q16, Q17, Q18, Q19, Q20, Q21, Q22, Q23, Q24, Q25, Q26, Q27, Q28, Q29, Q30, Q31, Q32, Q33, Q34, Q35]), "depth" : 25 * mm});
        }
        {
            var Q0;
            {var subQ0=sQuery(id+"F0.wireOp",EDGE,"E6.2.22");Q0=makeQuery(id+"F2.opExtrude","SWEPT_FACE",FACE,{"disambiguationData":[OSD([subQ0]),TDD([makeQuery(id+"F0.imprint","IMPRINT",EDGE,{"disambiguationData":[TD([[makeQuery(id+"F0.imprint","INTERSECT",VERTEX,{"derivedFrom":[subQ0,sQuery(id+"F0.wireOp",EDGE,"E6.2.32")]}),1.0]])],"derivedFrom":subQ0})])]});}
            var Q1;
            {var subQ0=sQuery(id+"F0.wireOp",EDGE,"E5.2.7");Q1=makeQuery(id+"F2.opExtrude","SWEPT_FACE",FACE,{"disambiguationData":[OSD([subQ0]),TDD([makeQuery(id+"F0.imprint","IMPRINT",EDGE,{"disambiguationData":[TD([[makeQuery(id+"F0.imprint","INTERSECT",VERTEX,{"derivedFrom":[subQ0,sQuery(id+"F0.wireOp",EDGE,"E5.2.9")]}),1.0]])],"derivedFrom":subQ0})])]});}
            var Q2;
            {var subQ0=sQuery(id+"F0.wireOp",EDGE,"E5.2.13");Q2=makeQuery(id+"F2.opExtrude","SWEPT_FACE",FACE,{"disambiguationData":[OSD([subQ0]),TDD([makeQuery(id+"F0.imprint","IMPRINT",EDGE,{"disambiguationData":[TD([[makeQuery(id+"F0.imprint","INTERSECT",VERTEX,{"derivedFrom":[sQuery(id+"F0.wireOp",EDGE,"E5.2.2"),subQ0]}),1.0]])],"derivedFrom":subQ0})])]});}
            var Q3;
            {var subQ0=sQuery(id+"F0.wireOp",EDGE,"E5.2.19");Q3=makeQuery(id+"F2.opExtrude","SWEPT_FACE",FACE,{"disambiguationData":[OSD([subQ0]),TDD([makeQuery(id+"F0.imprint","IMPRINT",EDGE,{"disambiguationData":[TD([[makeQuery(id+"F0.imprint","INTERSECT",VERTEX,{"derivedFrom":[subQ0,sQuery(id+"F0.wireOp",EDGE,"E5.2.5")]}),1.0]])],"derivedFrom":subQ0})])]});}
            var Q4;
            {var subQ0=sQuery(id+"F0.wireOp",EDGE,"E5.1.14");Q4=makeQuery(id+"F2.opExtrude","SWEPT_FACE",FACE,{"disambiguationData":[OSD([subQ0]),TDD([makeQuery(id+"F0.imprint","IMPRINT",EDGE,{"disambiguationData":[TD([[makeQuery(id+"F0.imprint","INTERSECT",VERTEX,{"derivedFrom":[sQuery(id+"F0.wireOp",EDGE,"E5.1.15"),subQ0]}),1.0]])],"derivedFrom":subQ0})])]});}
            var Q5;
            {var subQ0=sQuery(id+"F0.wireOp",EDGE,"E4.2.1");Q5=makeQuery(id+"F2.opExtrude","SWEPT_FACE",FACE,{"disambiguationData":[OSD([subQ0]),TDD([makeQuery(id+"F0.imprint","IMPRINT",EDGE,{"disambiguationData":[TD([[makeQuery(id+"F0.imprint","INTERSECT",VERTEX,{"derivedFrom":[subQ0,sQuery(id+"F0.wireOp",EDGE,"E4.2.0")]}),1.0]])],"derivedFrom":subQ0})])]});}
            var Q6;
            {var subQ0=sQuery(id+"F0.wireOp",EDGE,"E4.1.5");Q6=makeQuery(id+"F2.opExtrude","SWEPT_FACE",FACE,{"disambiguationData":[OSD([subQ0]),TDD([makeQuery(id+"F0.imprint","IMPRINT",EDGE,{"disambiguationData":[TD([[makeQuery(id+"F0.imprint","INTERSECT",VERTEX,{"derivedFrom":[subQ0,sQuery(id+"F0.wireOp",EDGE,"E4.1.7")]}),1.0]])],"derivedFrom":subQ0})])]});}
            var Q7;
            {var subQ0=sQuery(id+"F0.wireOp",EDGE,"E3.2.2");Q7=makeQuery(id+"F2.opExtrude","SWEPT_FACE",FACE,{"disambiguationData":[OSD([subQ0]),TDD([makeQuery(id+"F0.imprint","IMPRINT",EDGE,{"disambiguationData":[TD([[makeQuery(id+"F0.imprint","INTERSECT",VERTEX,{"derivedFrom":[subQ0,sQuery(id+"F0.wireOp",EDGE,"E3.2.1")]}),1.0]])],"derivedFrom":subQ0})])]});}
            var Q8;
            {var subQ0=sQuery(id+"F0.wireOp",EDGE,"E6.2.48");Q8=makeQuery(id+"F2.opExtrude","SWEPT_FACE",FACE,{"disambiguationData":[OSD([subQ0]),TDD([makeQuery(id+"F0.imprint","IMPRINT",EDGE,{"disambiguationData":[TD([[makeQuery(id+"F0.imprint","INTERSECT",VERTEX,{"derivedFrom":[sQuery(id+"F0.wireOp",EDGE,"E6.2.13"),subQ0]}),1.0]])],"derivedFrom":subQ0})])]});}
            var Q9;
            {var subQ0=sQuery(id+"F0.wireOp",EDGE,"E6.2.58");Q9=makeQuery(id+"F2.opExtrude","SWEPT_FACE",FACE,{"disambiguationData":[OSD([subQ0]),TDD([makeQuery(id+"F0.imprint","IMPRINT",EDGE,{"disambiguationData":[TD([[makeQuery(id+"F0.imprint","INTERSECT",VERTEX,{"derivedFrom":[sQuery(id+"F0.wireOp",EDGE,"E6.2.55"),subQ0]}),1.0]])],"derivedFrom":subQ0})])]});}
            var Q10;
            {var subQ0=sQuery(id+"F0.wireOp",EDGE,"E6.2.14");Q10=makeQuery(id+"F2.opExtrude","SWEPT_FACE",FACE,{"disambiguationData":[OSD([subQ0]),TDD([makeQuery(id+"F0.imprint","IMPRINT",EDGE,{"disambiguationData":[TD([[makeQuery(id+"F0.imprint","INTERSECT",VERTEX,{"derivedFrom":[subQ0,sQuery(id+"F0.wireOp",EDGE,"E6.2.34")]}),1.0]])],"derivedFrom":subQ0})])]});}
            var Q11;
            {var subQ0=sQuery(id+"F0.wireOp",EDGE,"E6.2.57");Q11=makeQuery(id+"F2.opExtrude","SWEPT_FACE",FACE,{"disambiguationData":[OSD([subQ0]),TDD([makeQuery(id+"F0.imprint","IMPRINT",EDGE,{"disambiguationData":[TD([[makeQuery(id+"F0.imprint","INTERSECT",VERTEX,{"derivedFrom":[sQuery(id+"F0.wireOp",EDGE,"E6.2.54"),subQ0]}),1.0]])],"derivedFrom":subQ0})])]});}
            var Q12;
            {var subQ0=sQuery(id+"F0.wireOp",EDGE,"E6.2.23");Q12=makeQuery(id+"F2.opExtrude","SWEPT_FACE",FACE,{"disambiguationData":[OSD([subQ0]),TDD([makeQuery(id+"F0.imprint","IMPRINT",EDGE,{"disambiguationData":[TD([[makeQuery(id+"F0.imprint","INTERSECT",VERTEX,{"derivedFrom":[subQ0,sQuery(id+"F0.wireOp",EDGE,"E6.2.24")]}),1.0]])],"derivedFrom":subQ0})])]});}
            var Q13;
            {var subQ0=sQuery(id+"F0.wireOp",EDGE,"E6.2.30");Q13=makeQuery(id+"F2.opExtrude","SWEPT_FACE",FACE,{"disambiguationData":[OSD([subQ0]),TDD([makeQuery(id+"F0.imprint","IMPRINT",EDGE,{"disambiguationData":[TD([[makeQuery(id+"F0.imprint","INTERSECT",VERTEX,{"derivedFrom":[sQuery(id+"F0.wireOp",EDGE,"E6.2.29"),subQ0]}),1.0]])],"derivedFrom":subQ0})])]});}
            var Q14;
            {var subQ0=sQuery(id+"F0.wireOp",EDGE,"E5.2.14");Q14=makeQuery(id+"F2.opExtrude","SWEPT_FACE",FACE,{"disambiguationData":[OSD([subQ0]),TDD([makeQuery(id+"F0.imprint","IMPRINT",EDGE,{"disambiguationData":[TD([[makeQuery(id+"F0.imprint","INTERSECT",VERTEX,{"derivedFrom":[sQuery(id+"F0.wireOp",EDGE,"E5.2.15"),subQ0]}),1.0]])],"derivedFrom":subQ0})])]});}
            var Q15;
            {var subQ0=sQuery(id+"F0.wireOp",EDGE,"E5.1.4");Q15=makeQuery(id+"F2.opExtrude","SWEPT_FACE",FACE,{"disambiguationData":[OSD([subQ0]),TDD([makeQuery(id+"F0.imprint","IMPRINT",EDGE,{"disambiguationData":[TD([[makeQuery(id+"F0.imprint","INTERSECT",VERTEX,{"derivedFrom":[sQuery(id+"F0.wireOp",EDGE,"E5.1.6"),subQ0]}),1.0]])],"derivedFrom":subQ0})])]});}
            var Q16;
            {var subQ0=sQuery(id+"F0.wireOp",EDGE,"E5.1.3");Q16=makeQuery(id+"F2.opExtrude","SWEPT_FACE",FACE,{"disambiguationData":[OSD([subQ0]),TDD([makeQuery(id+"F0.imprint","IMPRINT",EDGE,{"disambiguationData":[TD([[makeQuery(id+"F0.imprint","INTERSECT",VERTEX,{"derivedFrom":[subQ0,sQuery(id+"F0.wireOp",EDGE,"E5.1.1")]}),1.0]])],"derivedFrom":subQ0})])]});}
            var Q17;
            {var subQ0=sQuery(id+"F0.wireOp",EDGE,"E4.2.5");Q17=makeQuery(id+"F2.opExtrude","SWEPT_FACE",FACE,{"disambiguationData":[OSD([subQ0]),TDD([makeQuery(id+"F0.imprint","IMPRINT",EDGE,{"disambiguationData":[TD([[makeQuery(id+"F0.imprint","INTERSECT",VERTEX,{"derivedFrom":[subQ0,sQuery(id+"F0.wireOp",EDGE,"E4.2.7")]}),1.0]])],"derivedFrom":subQ0})])]});}
            var Q18;
            {var subQ0=sQuery(id+"F0.wireOp",EDGE,"E4.1.3");Q18=makeQuery(id+"F2.opExtrude","SWEPT_FACE",FACE,{"disambiguationData":[OSD([subQ0]),TDD([makeQuery(id+"F0.imprint","IMPRINT",EDGE,{"disambiguationData":[TD([[makeQuery(id+"F0.imprint","INTERSECT",VERTEX,{"derivedFrom":[subQ0,sQuery(id+"F0.wireOp",EDGE,"E4.1.6")]}),1.0]])],"derivedFrom":subQ0})])]});}
            var Q19;
            {var subQ0=sQuery(id+"F0.wireOp",EDGE,"E3.1.2");Q19=makeQuery(id+"F2.opExtrude","SWEPT_FACE",FACE,{"disambiguationData":[OSD([subQ0]),TDD([makeQuery(id+"F0.imprint","IMPRINT",EDGE,{"disambiguationData":[TD([[makeQuery(id+"F0.imprint","INTERSECT",VERTEX,{"derivedFrom":[sQuery(id+"F0.wireOp",EDGE,"E3.1.1"),subQ0]}),1.0]])],"derivedFrom":subQ0})])]});}
            var Q20;
            {var subQ0=sQuery(id+"F0.wireOp",EDGE,"E6.2.2");Q20=makeQuery(id+"F2.opExtrude","SWEPT_FACE",FACE,{"disambiguationData":[OSD([subQ0]),TDD([makeQuery(id+"F0.imprint","IMPRINT",EDGE,{"disambiguationData":[TD([[makeQuery(id+"F0.imprint","INTERSECT",VERTEX,{"derivedFrom":[subQ0,sQuery(id+"F0.wireOp",EDGE,"E6.2.43")]}),1.0]])],"derivedFrom":subQ0})])]});}
            var Q21;
            {var subQ0=sQuery(id+"F0.wireOp",EDGE,"E6.2.45");Q21=makeQuery(id+"F2.opExtrude","SWEPT_FACE",FACE,{"disambiguationData":[OSD([subQ0]),TDD([makeQuery(id+"F0.imprint","IMPRINT",EDGE,{"disambiguationData":[TD([[makeQuery(id+"F0.imprint","INTERSECT",VERTEX,{"derivedFrom":[sQuery(id+"F0.wireOp",EDGE,"E6.2.1"),subQ0]}),1.0]])],"derivedFrom":subQ0})])]});}
            var Q22;
            {var subQ0=sQuery(id+"F0.wireOp",EDGE,"E6.2.44");Q22=makeQuery(id+"F2.opExtrude","SWEPT_FACE",FACE,{"disambiguationData":[OSD([subQ0]),TDD([makeQuery(id+"F0.imprint","IMPRINT",EDGE,{"disambiguationData":[TD([[makeQuery(id+"F0.imprint","INTERSECT",VERTEX,{"derivedFrom":[sQuery(id+"F0.wireOp",EDGE,"E6.2.5"),subQ0]}),1.0]])],"derivedFrom":subQ0})])]});}
            var Q23;
            {var subQ0=sQuery(id+"F0.wireOp",EDGE,"E6.2.59");Q23=makeQuery(id+"F2.opExtrude","SWEPT_FACE",FACE,{"disambiguationData":[OSD([subQ0]),TDD([makeQuery(id+"F0.imprint","IMPRINT",EDGE,{"disambiguationData":[TD([[makeQuery(id+"F0.imprint","INTERSECT",VERTEX,{"derivedFrom":[sQuery(id+"F0.wireOp",EDGE,"E6.2.56"),subQ0]}),1.0]])],"derivedFrom":subQ0})])]});}
            var Q24;
            {var subQ0=sQuery(id+"F0.wireOp",EDGE,"E6.2.33");Q24=makeQuery(id+"F2.opExtrude","SWEPT_FACE",FACE,{"disambiguationData":[OSD([subQ0]),TDD([makeQuery(id+"F0.imprint","IMPRINT",EDGE,{"disambiguationData":[TD([[makeQuery(id+"F0.imprint","INTERSECT",VERTEX,{"derivedFrom":[sQuery(id+"F0.wireOp",EDGE,"E6.2.31"),subQ0]}),1.0]])],"derivedFrom":subQ0})])]});}
            var Q25;
            {var subQ0=sQuery(id+"F0.wireOp",EDGE,"E5.2.4");Q25=makeQuery(id+"F2.opExtrude","SWEPT_FACE",FACE,{"disambiguationData":[OSD([subQ0]),TDD([makeQuery(id+"F0.imprint","IMPRINT",EDGE,{"disambiguationData":[TD([[makeQuery(id+"F0.imprint","INTERSECT",VERTEX,{"derivedFrom":[subQ0,sQuery(id+"F0.wireOp",EDGE,"E5.2.6")]}),1.0]])],"derivedFrom":subQ0})])]});}
            var Q26;
            {var subQ0=sQuery(id+"F0.wireOp",EDGE,"E5.2.3");Q26=makeQuery(id+"F2.opExtrude","SWEPT_FACE",FACE,{"disambiguationData":[OSD([subQ0]),TDD([makeQuery(id+"F0.imprint","IMPRINT",EDGE,{"disambiguationData":[TD([[makeQuery(id+"F0.imprint","INTERSECT",VERTEX,{"derivedFrom":[sQuery(id+"F0.wireOp",EDGE,"E5.2.1"),subQ0]}),1.0]])],"derivedFrom":subQ0})])]});}
            var Q27;
            {var subQ0=sQuery(id+"F0.wireOp",EDGE,"E5.1.7");Q27=makeQuery(id+"F2.opExtrude","SWEPT_FACE",FACE,{"disambiguationData":[OSD([subQ0]),TDD([makeQuery(id+"F0.imprint","IMPRINT",EDGE,{"disambiguationData":[TD([[makeQuery(id+"F0.imprint","INTERSECT",VERTEX,{"derivedFrom":[subQ0,sQuery(id+"F0.wireOp",EDGE,"E5.1.9")]}),1.0]])],"derivedFrom":subQ0})])]});}
            var Q28;
            {var subQ0=sQuery(id+"F0.wireOp",EDGE,"E5.1.13");Q28=makeQuery(id+"F2.opExtrude","SWEPT_FACE",FACE,{"disambiguationData":[OSD([subQ0]),TDD([makeQuery(id+"F0.imprint","IMPRINT",EDGE,{"disambiguationData":[TD([[makeQuery(id+"F0.imprint","INTERSECT",VERTEX,{"derivedFrom":[subQ0,sQuery(id+"F0.wireOp",EDGE,"E5.1.2")]}),1.0]])],"derivedFrom":subQ0})])]});}
            var Q29;
            {var subQ0=sQuery(id+"F0.wireOp",EDGE,"E4.2.3");Q29=makeQuery(id+"F2.opExtrude","SWEPT_FACE",FACE,{"disambiguationData":[OSD([subQ0]),TDD([makeQuery(id+"F0.imprint","IMPRINT",EDGE,{"disambiguationData":[TD([[makeQuery(id+"F0.imprint","INTERSECT",VERTEX,{"derivedFrom":[sQuery(id+"F0.wireOp",EDGE,"E4.2.6"),subQ0]}),1.0]])],"derivedFrom":subQ0})])]});}
            var Q30;
            {var subQ0=sQuery(id+"F0.wireOp",EDGE,"E4.1.1");Q30=makeQuery(id+"F2.opExtrude","SWEPT_FACE",FACE,{"disambiguationData":[OSD([subQ0]),TDD([makeQuery(id+"F0.imprint","IMPRINT",EDGE,{"disambiguationData":[TD([[makeQuery(id+"F0.imprint","INTERSECT",VERTEX,{"derivedFrom":[sQuery(id+"F0.wireOp",EDGE,"E4.1.0"),subQ0]}),1.0]])],"derivedFrom":subQ0})])]});}
            var Q31;
            {var subQ0=sQuery(id+"F0.wireOp",EDGE,"E1");Q31=makeQuery(id+"F2.opExtrude","SWEPT_FACE",FACE,{"disambiguationData":[OSD([subQ0]),TDD([makeQuery(id+"F0.imprint","IMPRINT",EDGE,{"disambiguationData":[TD([[makeQuery(id+"F0.imprint","INTERSECT",VERTEX,{"derivedFrom":[subQ0,sQuery(id+"F0.wireOp",EDGE,"E2")]}),1.0]])],"derivedFrom":subQ0})])]});}
            var Q32;
            {var subQ0=sQuery(id+"F0.wireOp",EDGE,"E6.2.40");Q32=makeQuery(id+"F2.opExtrude","SWEPT_FACE",FACE,{"disambiguationData":[OSD([subQ0]),TDD([makeQuery(id+"F0.imprint","IMPRINT",EDGE,{"disambiguationData":[TD([[makeQuery(id+"F0.imprint","INTERSECT",VERTEX,{"derivedFrom":[sQuery(id+"F0.wireOp",EDGE,"E6.2.36"),subQ0]}),1.0]])],"derivedFrom":subQ0})])]});}
            var Q33;
            {var subQ0=sQuery(id+"F0.wireOp",EDGE,"E6.2.53");Q33=makeQuery(id+"F2.opExtrude","SWEPT_FACE",FACE,{"disambiguationData":[OSD([subQ0]),TDD([makeQuery(id+"F0.imprint","IMPRINT",EDGE,{"disambiguationData":[TD([[makeQuery(id+"F0.imprint","INTERSECT",VERTEX,{"derivedFrom":[subQ0,sQuery(id+"F0.wireOp",EDGE,"E6.2.60")]}),1.0]])],"derivedFrom":subQ0})])]});}
            var Q34;
            {var subQ0=sQuery(id+"F0.wireOp",EDGE,"E6.2.19");Q34=makeQuery(id+"F2.opExtrude","SWEPT_FACE",FACE,{"disambiguationData":[OSD([subQ0]),TDD([makeQuery(id+"F0.imprint","IMPRINT",EDGE,{"disambiguationData":[TD([[makeQuery(id+"F0.imprint","INTERSECT",VERTEX,{"derivedFrom":[subQ0,sQuery(id+"F0.wireOp",EDGE,"E6.2.39")]}),1.0]])],"derivedFrom":subQ0})])]});}
            var Q35;
            {var subQ0=sQuery(id+"F0.wireOp",EDGE,"E6.2.50");Q35=makeQuery(id+"F2.opExtrude","SWEPT_FACE",FACE,{"disambiguationData":[OSD([subQ0]),TDD([makeQuery(id+"F0.imprint","IMPRINT",EDGE,{"disambiguationData":[TD([[makeQuery(id+"F0.imprint","INTERSECT",VERTEX,{"derivedFrom":[sQuery(id+"F0.wireOp",EDGE,"E6.2.49"),subQ0]}),1.0]])],"derivedFrom":subQ0})])]});}
            fillet(context, id + "F3", {"entities" : qUnion([Q0, Q1, Q2, Q3, Q4, Q5, Q6, Q7, Q8, Q9, Q10, Q11, Q12, Q13, Q14, Q15, Q16, Q17, Q18, Q19, Q20, Q21, Q22, Q23, Q24, Q25, Q26, Q27, Q28, Q29, Q30, Q31, Q32, Q33, Q34, Q35]), "radius" : 1.59 * mm, "tangentPropagation" : true, "allowEdgeOverflow" : false});
        }
    });
